# Revit family: Bernhardt_Design-Tables-Conference-Matera
name_source: partatom
category: Furniture
revit_build: Autodesk Revit 2016 (Build: 20150714_1515(x64)
units: mm (PartAtom-declared; Revit-internal decimal feet)

## family parameters
Always vertical = Yes
Cut with Voids When Loaded = No
OmniClass Number = 23.40.20.00
OmniClass Title = General Furniture and Specialties
Room Calculation Point = No
Shared = No
Work Plane-Based = No

## types (19) — shared parameters
Legs = <By Category>
Manufacturer = Bernhardt Design
Model = Matera
TableTop = <By Category>
URL = http://www.bernhardtdesign.com

## per-type parameters (varying)
| type | Catalog | SKU | fourthLeg_visibility | railWidth | tableLength | tableWidth | thirdLeg_visibility |
| Matera - E3D 204x54 | E3D | E3D | No | 80 3/8" | 102" | 27" | Yes |
| Matera - E3E 204x60 | E3E | E3E | No | 80 3/8" | 102" | 30" | Yes |
| Matera - E9D 240x54 | E9D | E9D | Yes | 98 3/8" | 120" | 27" | No |
| Matera - E9E 240x60 | E9E | E9E | Yes | 98 3/8" | 120" | 30" | No |
| Matera - EGC 72x48 | EGC | EGC | No | 14 3/8" | 36" | 24" | No |
| Matera - EKC 96x48 | EKC | EKC | No | 26 3/8" | 48" | 24" | No |
| Matera - EKD 96x54 | EKD | EKD | No | 26 3/8" | 48" | 27" | No |
| Matera - EKE 96x60 | EKE | EKE | No | 26 3/8" | 48" | 30" | No |
| Matera - EMC 108x48 | EMC | EMC | No | 32 3/8" | 54" | 24" | No |
| Matera - EMD 108x54 | EMD | EMD | No | 32 3/8" | 54" | 27" | No |
| Matera - EME 108x60 | EME | EME | No | 32 3/8" | 54" | 30" | No |
| Matera - EOC 120x48 | EOC | EOC | No | 38 3/8" | 60" | 24" | No |
| Matera - EOD 120x54 | EOD | EOD | No | 38 3/8" | 60" | 27" | No |
| Matera - EOE 120x60 | EOE | EOE | No | 38 3/8" | 60" | 30" | No |
| Matera - EQC 132x48 | EQC | EQC | No | 44 3/8" | 66" | 24" | Yes |
| Matera - EQD 132x54 | EQD | EQD | No | 44 3/8" | 66" | 27" | Yes |
| Matera - EQE 132x60 | EQE | EQE | No | 44 3/8" | 66" | 30" | Yes |
| Matera - EWD 168x54 | EWD | EWD | No | 62 3/8" | 84" | 27" | Yes |
| Matera - EWE 168x60 | EWE | EWE | No | 62 3/8" | 84" | 30" | Yes |

## geometry (parser evidence)
native form markers: Sweep x1
no freeform markers — native parametric forms only
